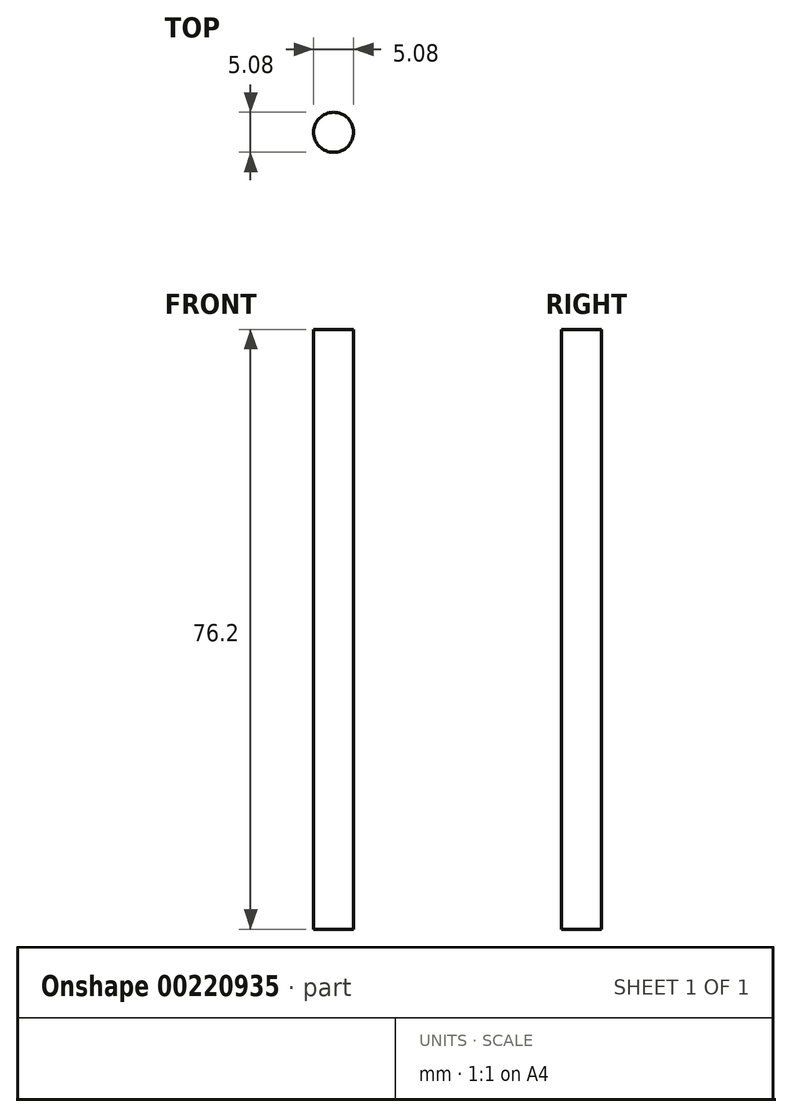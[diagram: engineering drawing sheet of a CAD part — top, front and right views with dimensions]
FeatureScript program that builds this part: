
annotation { "Feature Type Name" : "Feature", "Feature Type Description" : "" }
export const myFeature = defineFeature(function(context is Context, id is Id, definition is map)
    precondition{}
    {
        {
            var Q0;
            Q0=qCreatedBy(makeId("Top.planeOp"),FACE);
            var sketch = newSketch(context, id + "F0", { "sketchPlane" : qUnion([Q0])});
            skCircle(sketch, "E0", {"center": v(0, 0) * mm, "radius": 2.54 * mm});
            skSolve(sketch);
        }
        {
            var Q0;
            Q0 = qSketchRegion(id + "F0", true);
            extrude(context, id + "F1", {"entities" : qUnion([Q0]), "depth" : 76.2 * mm});
        }
    });
